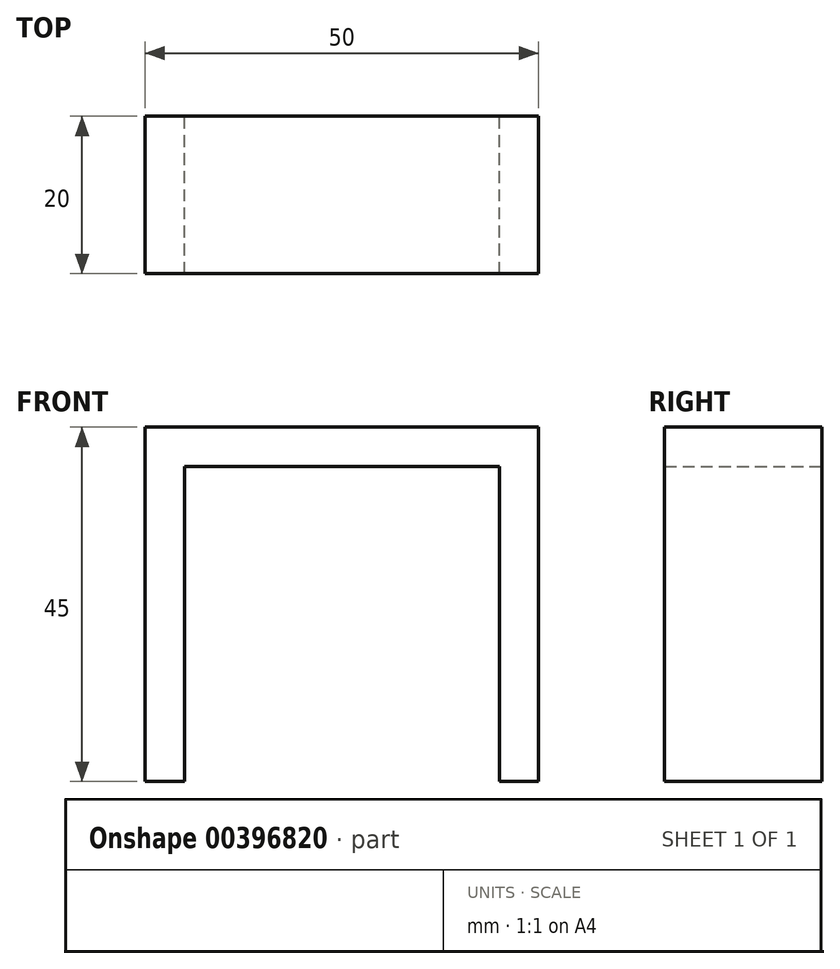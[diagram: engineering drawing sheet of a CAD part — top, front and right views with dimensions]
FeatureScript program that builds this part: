
annotation { "Feature Type Name" : "Feature", "Feature Type Description" : "" }
export const myFeature = defineFeature(function(context is Context, id is Id, definition is map)
    precondition{}
    {
        {
            var Q0;
            Q0=qCreatedBy(makeId("Front.planeOp"),FACE);
            var sketch = newSketch(context, id + "F0", { "sketchPlane" : qUnion([Q0])});
            skLineSegment(sketch, "E0.bottom", {"start": v(25, 0) * mm, "end": v(-25, 0) * mm});
            skLineSegment(sketch, "E0.top", {"start": v(25, 45) * mm, "end": v(-25, 45) * mm});
            skLineSegment(sketch, "E0.left", {"start": v(25, 0) * mm, "end": v(25, 45) * mm});
            skLineSegment(sketch, "E0.right", {"start": v(-25, 0) * mm, "end": v(-25, 45) * mm});
            skSolve(sketch);
        }
        {
            var Q0;
            Q0=makeQuery(id+"F0.imprint","IMPRINT",FACE,{"disambiguationData":[TD([[makeQuery(id+"F0.imprint","IMPRINT",EDGE,{"derivedFrom":sQuery(id+"F0.wireOp",EDGE,"E0.bottom")}),-1.0]])]});
            extrude(context, id + "F1", {"entities" : qUnion([Q0]), "depth" : 20 * mm});
        }
        {
            var Q0;
            Q0=qCreatedBy(makeId("Front.planeOp"),FACE);
            var sketch = newSketch(context, id + "F2", { "sketchPlane" : qUnion([Q0])});
            skLineSegment(sketch, "E1.bottom", {"start": v(20, -40) * mm, "end": v(-20, -40) * mm});
            skLineSegment(sketch, "E1.top", {"start": v(20, 40) * mm, "end": v(-20, 40) * mm});
            skLineSegment(sketch, "E1.left", {"start": v(20, -40) * mm, "end": v(20, 40) * mm});
            skLineSegment(sketch, "E1.right", {"start": v(-20, -40) * mm, "end": v(-20, 40) * mm});
            skPoint(sketch, "E1.middle", {"position": v(0, 0) * mm});
            skSolve(sketch);
        }
        {
            var Q0;
            Q0 = qSketchRegion(id + "F2", true);
            extrude(context, id + "F3", {"entities" : qUnion([Q0]), "operationType" : NewBodyOperationType.REMOVE, "depth" : 20 * mm});
        }
    });
